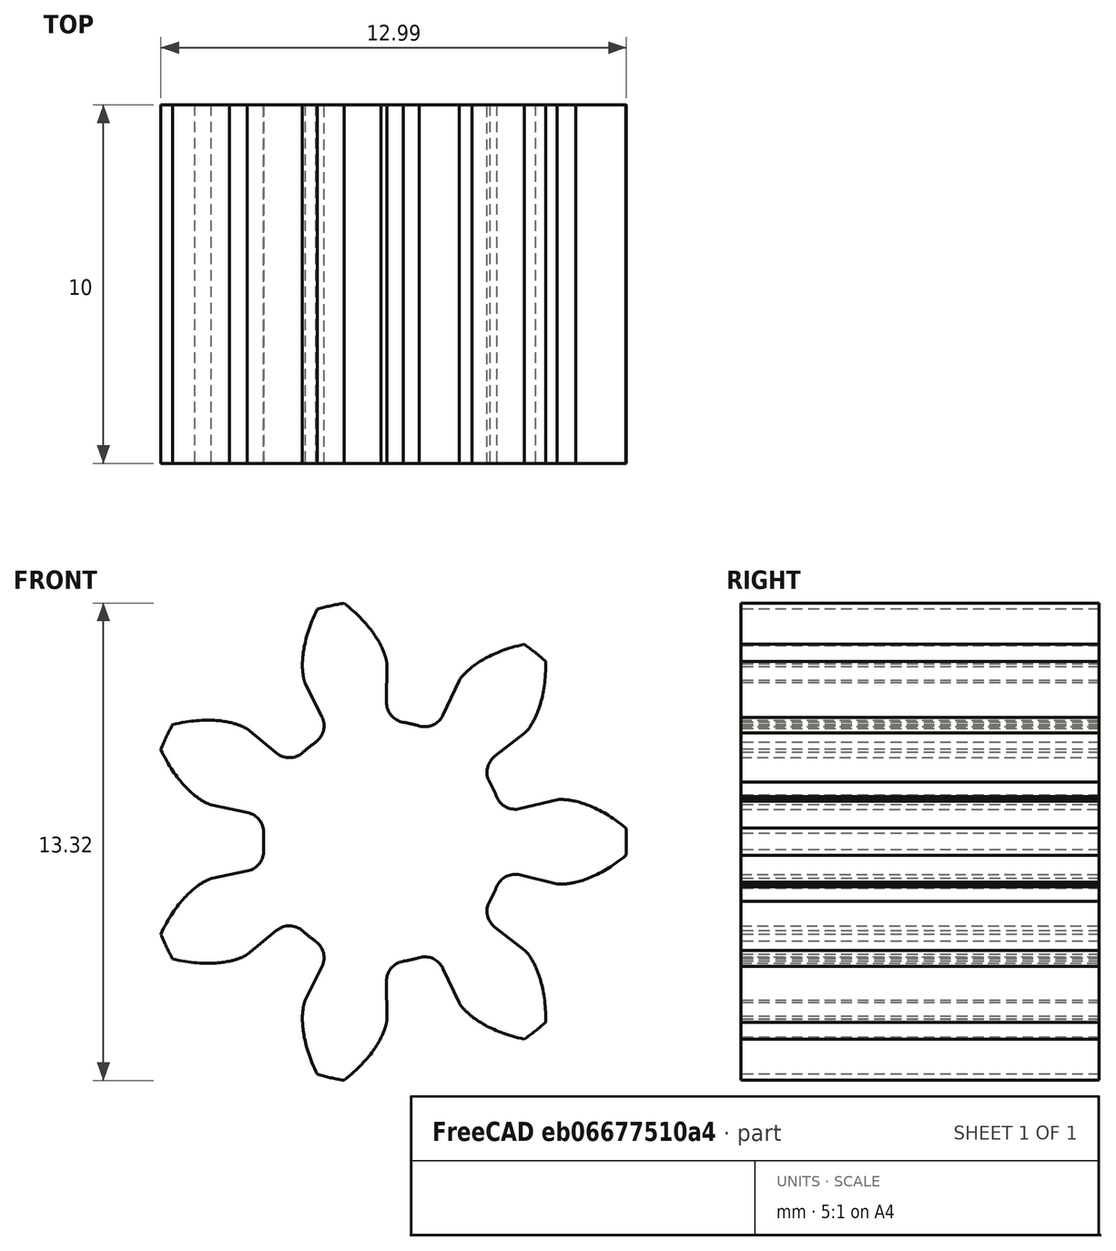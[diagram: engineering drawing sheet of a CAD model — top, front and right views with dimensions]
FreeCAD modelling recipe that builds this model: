
FCSTD DOCUMENT  (FreeCAD 0.16R6705 (Git))
Label: bubuplex
License: All rights reserved
LicenseURL: http://it.wikipedia.org/wiki/<copyright redacted>
objects: Part::Part2DObjectPython×1, PartDesign::Pad×1, Sketcher::SketchObject×1, PartDesign::Pocket×1, Part::MultiFuse×1
note: 7 computed .brp shape members not serialized (recipe doc carries the construction recipe); baked Part::Feature solids carry a one-line shape summary decoded from their .brp

FEATURE [Part::Part2DObjectPython] InvoluteGear001  # Draft 2D object (typed FeaturePython)
  ExternalGear = true
  HighPrecision = true
  Modules = 1.5
  NumberOfTeeth = 7
  Placement = pos=(16,0,0) rot=(1,0,0;1.5708rad)
  PressureAngle = 20
FEATURE [PartDesign::Pad] Pad003  label="ruota_dentata_motore"
  Length = 10
  Length2 = 100
  Placement = pos=(16,0,0) rot=(1,0,0;1.5708rad)
  Sketch = -> InvoluteGear001
  Type = 0
FEATURE [Sketcher::SketchObject] Sketch012
  Placement = pos=(16,-10,0) rot=(1,0,0;1.5708rad)
  Support = -> Pad003 [Face72]
  sketch-geometry (3):
    g0: ArcOfCircle CenterX=0.00960217 CenterY=0.00978991 CenterZ=0 NormalX=0 NormalY=0 NormalZ=1 Radius=1.5 StartAngle=5.5029 EndAngle=10.2051
    g1: LineSegment StartX=-1.05646 StartY=-1.04544 StartZ=0 EndX=1.07567 EndY=-1.04544 EndZ=0
    g2: GeomPoint [constr] X=1.0761 Y=-1.19021 Z=0
  constraints (5):
    c: Radius(g0) = 1.5
    c: Parallel(g-1,g1)
    c: Coincident(g0,g1)
    c: Coincident(g0,g1)
    c: DistanceY(g2,g0) = 1.2
FEATURE [PartDesign::Pocket] Pocket
  Length = 5
  Placement = pos=(16,0,0) rot=(1,0,0;1.5708rad)
  Sketch = -> Sketch012
  Type = 1
FEATURE [Part::MultiFuse] Fusion004  label="ruota_dentata_motore_con_buco"
  Shapes = -> [Pocket,Pad003]
